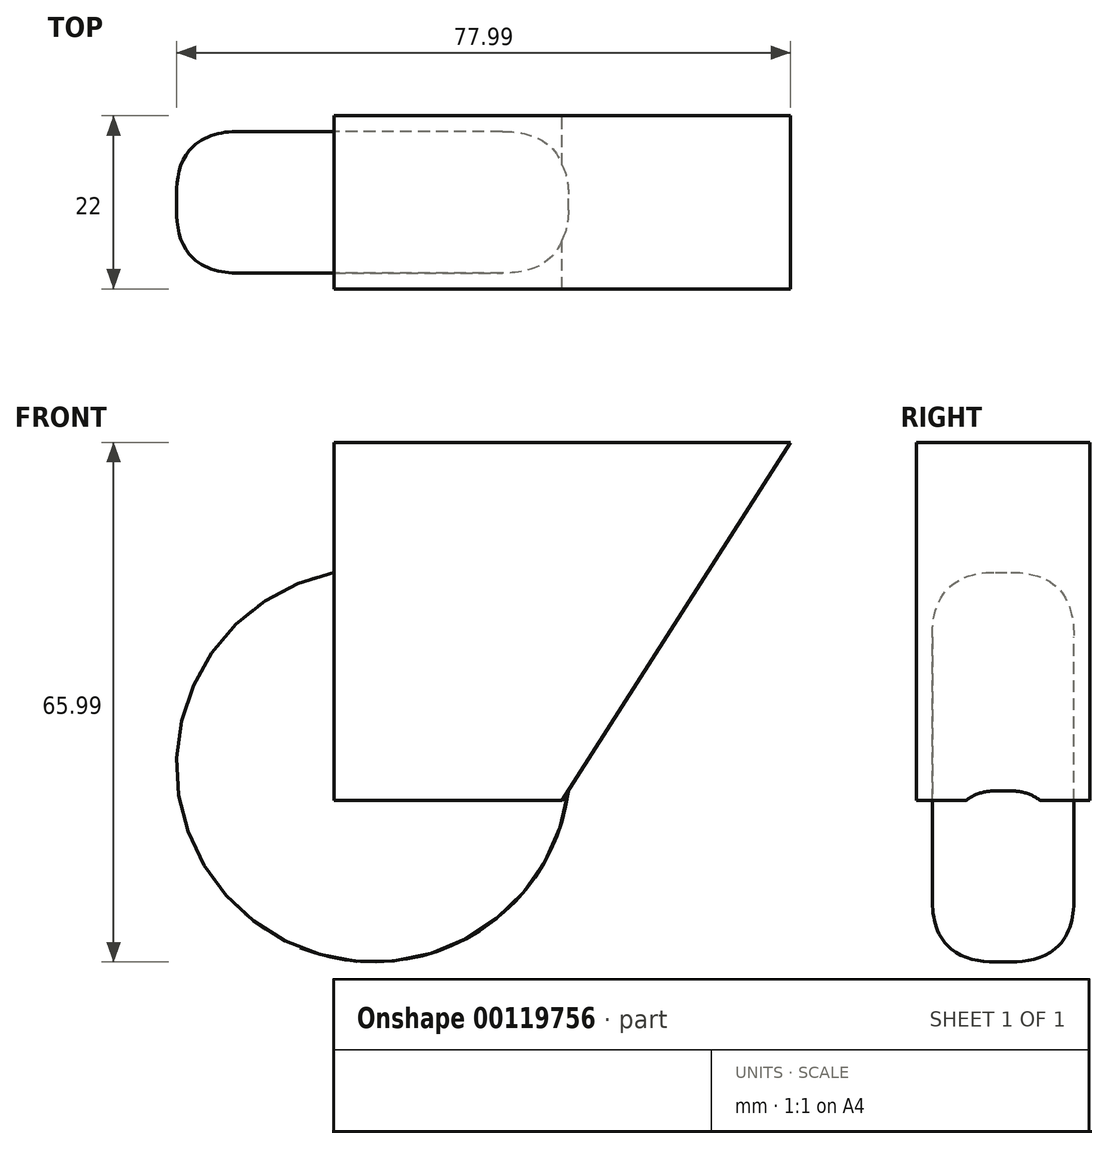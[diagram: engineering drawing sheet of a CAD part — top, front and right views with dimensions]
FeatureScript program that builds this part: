
annotation { "Feature Type Name" : "Feature", "Feature Type Description" : "" }
export const myFeature = defineFeature(function(context is Context, id is Id, definition is map)
    precondition{}
    {
        {
            var Q0;
            Q0=qCreatedBy(makeId("Front.planeOp"),FACE);
            var sketch = newSketch(context, id + "F0", { "sketchPlane" : qUnion([Q0])});
            skCircle(sketch, "E0", {"center": v(0, 0) * mm, "radius": 25 * mm});
            skSolve(sketch);
        }
        {
            var Q0;
            Q0=makeQuery(id+"F0.imprint","IMPRINT",FACE,{"disambiguationData":[TD([[makeQuery(id+"F0.imprint","IMPRINT",EDGE,{"derivedFrom":sQuery(id+"F0.wireOp",EDGE,"E0")}),1.0]])]});
            extrude(context, id + "F1", {"entities" : qUnion([Q0]), "endBound" : BoundingType.SYMMETRIC, "depth" : 18 * mm});
        }
        {
            var Q0;
            Q0=makeQuery(id+"F1.opExtrude","SWEPT_FACE",FACE,{"disambiguationData":[OSD([sQuery(id+"F0.wireOp",EDGE,"E0")])]});
            fillet(context, id + "F2", {"entities" : qUnion([Q0]), "radius" : 8 * mm, "rho" : 0.5, "crossSection" : FilletCrossSection.CONIC, "allowEdgeOverflow" : false});
        }
        {
            var Q0;
            Q0=qCreatedBy(makeId("Front.planeOp"),FACE);
            var sketch = newSketch(context, id + "F3", { "sketchPlane" : qUnion([Q0])});
            skLineSegment(sketch, "E1", {"start": v(-5, 41) * mm, "end": v(-5, -4.51) * mm});
            skLineSegment(sketch, "E2", {"start": v(-5, -4.51) * mm, "end": v(24, -4.51) * mm});
            skLineSegment(sketch, "E3", {"start": v(24, -4.51) * mm, "end": v(53, 41) * mm});
            skLineSegment(sketch, "E4", {"start": v(53, 41) * mm, "end": v(-5, 41) * mm});
            skLineSegment(sketch, "E5", {"start": v(24, 6.7) * mm, "end": v(24, 41) * mm, "construction": true});
            skSolve(sketch);
        }
        {
            var Q0;
            {var subQ1=sQuery(id+"F3.wireOp",EDGE,"E3");Q0=makeQuery(id+"F3.imprint","IMPRINT",FACE,{"disambiguationData":[TD([[makeQuery(id+"F3.imprint","IMPRINT",EDGE,{"derivedFrom":subQ1}),1.0]])]});}
            extrude(context, id + "F4", {"entities" : qUnion([Q0]), "operationType" : NewBodyOperationType.ADD, "endBound" : BoundingType.SYMMETRIC, "depth" : 22 * mm});
        }
    });
